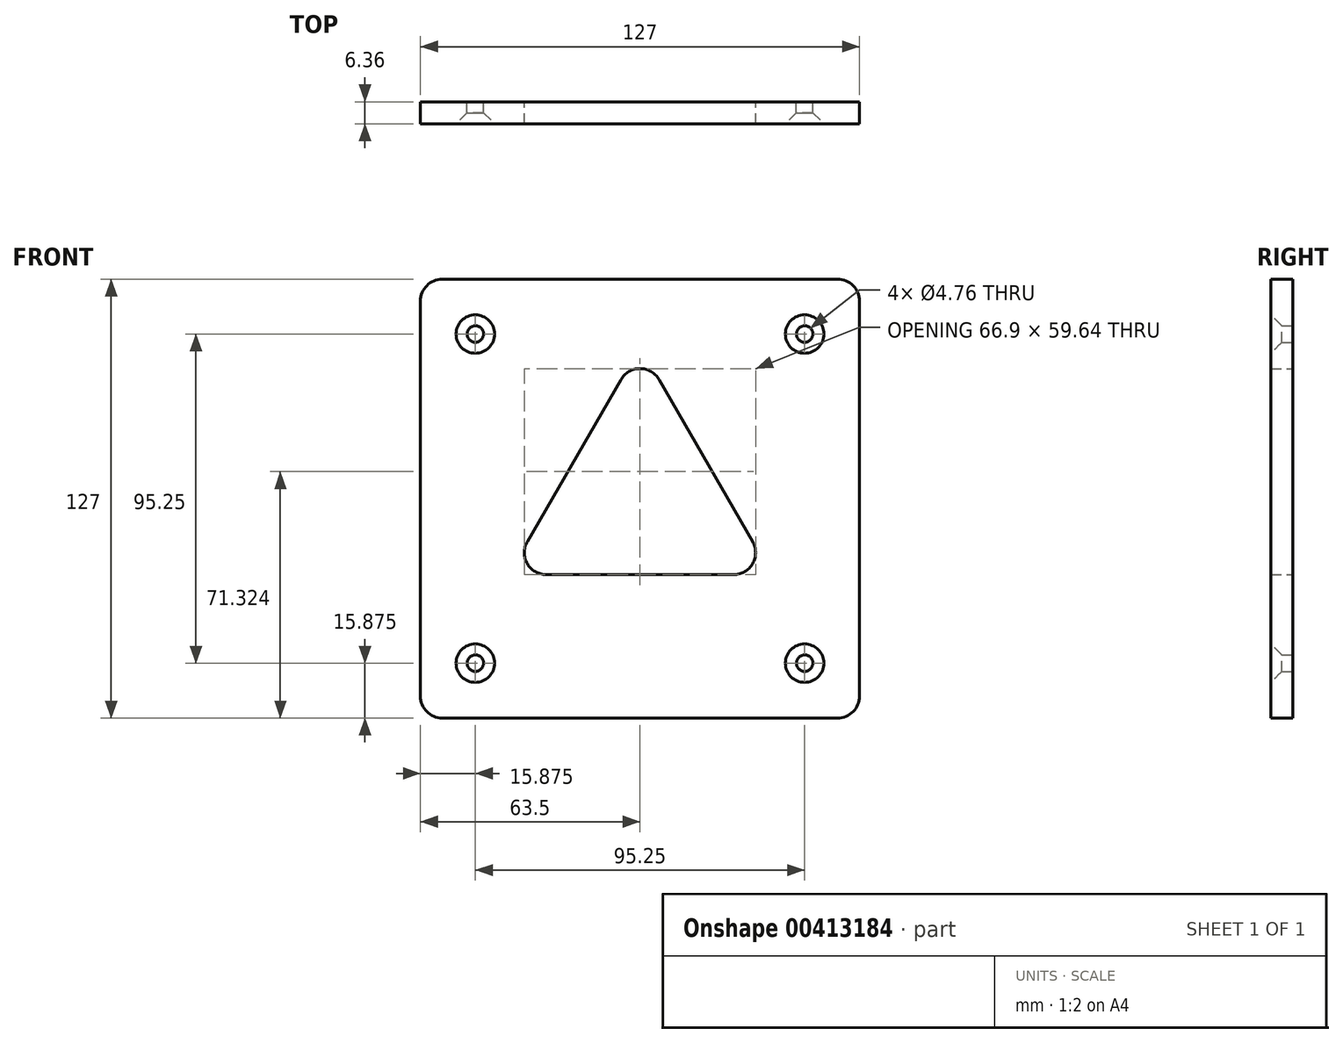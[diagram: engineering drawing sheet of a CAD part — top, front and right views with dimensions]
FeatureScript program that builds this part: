
annotation { "Feature Type Name" : "Feature", "Feature Type Description" : "" }
export const myFeature = defineFeature(function(context is Context, id is Id, definition is map)
    precondition{}
    {
        {
            var Q0;
            Q0=qCreatedBy(makeId("Front.planeOp"),FACE);
            var sketch = newSketch(context, id + "F0", { "sketchPlane" : qUnion([Q0])});
            skLineSegment(sketch, "E0.bottom", {"start": v(-57.15, 63.5) * mm, "end": v(57.15, 63.5) * mm});
            skLineSegment(sketch, "E0.top", {"start": v(-57.15, -63.5) * mm, "end": v(57.15, -63.5) * mm});
            skLineSegment(sketch, "E0.left", {"start": v(-63.5, 57.15) * mm, "end": v(-63.5, -57.15) * mm});
            skLineSegment(sketch, "E0.right", {"start": v(63.5, 57.15) * mm, "end": v(63.5, -57.15) * mm});
            skPoint(sketch, "E0.middle", {"position": v(0, 0) * mm});
            skLineSegment(sketch, "E1.bottom", {"start": v(-47.63, 47.63) * mm, "end": v(47.63, 47.63) * mm, "construction": true});
            skLineSegment(sketch, "E1.top", {"start": v(-47.63, -47.63) * mm, "end": v(47.63, -47.63) * mm, "construction": true});
            skLineSegment(sketch, "E1.left", {"start": v(-47.62, 47.63) * mm, "end": v(-47.63, -47.63) * mm, "construction": true});
            skLineSegment(sketch, "E1.right", {"start": v(47.63, 47.63) * mm, "end": v(47.63, -47.63) * mm, "construction": true});
            skLineSegment(sketch, "E2", {"start": v(-5.5, 34.47) * mm, "end": v(-32.6, -12.47) * mm});
            skLineSegment(sketch, "E3", {"start": v(-27.1, -22) * mm, "end": v(27.1, -22) * mm});
            skLineSegment(sketch, "E4", {"start": v(32.6, -12.47) * mm, "end": v(5.5, 34.47) * mm});
            skLineSegment(sketch, "E5", {"start": v(0, 0) * mm, "end": v(0, -22) * mm, "construction": true});
            skLineSegment(sketch, "E6", {"start": v(0, 0) * mm, "end": v(-19.05, 11) * mm, "construction": true});
            skCircle(sketch, "E7", {"center": v(-47.63, 47.63) * mm, "radius": 2.38 * mm});
            skCircle(sketch, "E8", {"center": v(47.63, -47.63) * mm, "radius": 2.38 * mm});
            skCircle(sketch, "E9", {"center": v(-47.63, -47.63) * mm, "radius": 2.38 * mm});
            skCircle(sketch, "E10", {"center": v(47.63, 47.63) * mm, "radius": 2.38 * mm});
            skPoint(sketch, "E11.visualSharp", {"position": v(-38.1, -22) * mm});
            skArc(sketch, "E11.filletArc", {"start": v(-32.6, -12.47) * mm, "mid": v(-32.6, -18.82) * mm, "end": v(-27.1, -22) * mm});
            skPoint(sketch, "E12.visualSharp", {"position": v(38.1, -22) * mm});
            skArc(sketch, "E12.filletArc", {"start": v(27.1, -22) * mm, "mid": v(32.6, -18.82) * mm, "end": v(32.6, -12.47) * mm});
            skPoint(sketch, "E13.visualSharp", {"position": v(0, 44) * mm});
            skArc(sketch, "E13.filletArc", {"start": v(5.5, 34.47) * mm, "mid": v(0, 37.64) * mm, "end": v(-5.5, 34.47) * mm});
            skLineSegment(sketch, "E14", {"start": v(0, 0) * mm, "end": v(19.05, 11) * mm, "construction": true});
            skPoint(sketch, "E15.visualSharp", {"position": v(-63.5, 63.5) * mm});
            skArc(sketch, "E15.filletArc", {"start": v(-57.15, 63.5) * mm, "mid": v(-61.64, 61.64) * mm, "end": v(-63.5, 57.15) * mm});
            skPoint(sketch, "E16.visualSharp", {"position": v(63.5, 63.5) * mm});
            skArc(sketch, "E16.filletArc", {"start": v(63.5, 57.15) * mm, "mid": v(61.64, 61.64) * mm, "end": v(57.15, 63.5) * mm});
            skPoint(sketch, "E17.visualSharp", {"position": v(63.5, -63.5) * mm});
            skArc(sketch, "E17.filletArc", {"start": v(57.15, -63.5) * mm, "mid": v(61.64, -61.64) * mm, "end": v(63.5, -57.15) * mm});
            skPoint(sketch, "E18.visualSharp", {"position": v(-63.5, -63.5) * mm});
            skArc(sketch, "E18.filletArc", {"start": v(-63.5, -57.15) * mm, "mid": v(-61.64, -61.64) * mm, "end": v(-57.15, -63.5) * mm});
            skSolve(sketch);
        }
        {
            var Q0;
            Q0=makeQuery(id+"F0.imprint","IMPRINT",FACE,{"disambiguationData":[TD([[makeQuery(id+"F0.imprint","IMPRINT",EDGE,{"derivedFrom":sQuery(id+"F0.wireOp",EDGE,"E0.bottom")}),-1.0]])]});
            extrude(context, id + "F1", {"entities" : qUnion([Q0]), "endBound" : BoundingType.SYMMETRIC, "depth" : 6.35 * mm});
        }
        {
            var Q0;
            Q0=makeQuery(id+"F1.opExtrude","CAP_EDGE",EDGE,{"disambiguationData":[OSD([sQuery(id+"F0.wireOp",EDGE,"E7")])],"isStart":false});
            var Q1;
            Q1=makeQuery(id+"F1.opExtrude","CAP_EDGE",EDGE,{"disambiguationData":[OSD([sQuery(id+"F0.wireOp",EDGE,"E9")])],"isStart":false});
            var Q2;
            Q2=makeQuery(id+"F1.opExtrude","CAP_EDGE",EDGE,{"disambiguationData":[OSD([sQuery(id+"F0.wireOp",EDGE,"E8")])],"isStart":false});
            var Q3;
            Q3=makeQuery(id+"F1.opExtrude","CAP_EDGE",EDGE,{"disambiguationData":[OSD([sQuery(id+"F0.wireOp",EDGE,"E10")])],"isStart":false});
            chamfer(context, id + "F2", {"entities" : qUnion([Q0, Q1, Q2, Q3]), "width" : 3.17 * mm, "tangentPropagation" : true});
        }
    });
